# Revit family: Haworth_Encourage_Table
name_source: partatom
category: Furniture
revit_build: Autodesk Revit 2018 (Build: 20170223_1515(x64)
units: mm (PartAtom-declared; Revit-internal decimal feet)

## family parameters
Always vertical = Yes
Cut with Voids When Loaded = No
OmniClass Number = 23.40.70.14.64.21
OmniClass Title = Systems Furniture
Room Calculation Point = No
Shared = No
Work Plane-Based = No

## types (8) — shared parameters
Actual Height = 28 69/256"
Assembly Code = E2020200
Description = Haworth Encourage Table
Leg Finish = Haworth _ Metal _ Stainless Steel
Manufacturer = Haworth
Min/Max Depth = 48 in. / 60 in.
Min/Max Width = 96 in. / 180 in.
Model = TNBO
Power Trough = Yes
Revision Number = 4
Size = Verify Final Dim. w/ Haworth
Top Thickness = 1 27/256"
URL = http://www.haworth.com
URL - Product = https://www.haworth.com
Warranty = http://www.haworth.com

## per-type parameters (varying)
| type | 48d 108w | 48d 96w | 51d 120w | 54d 132w | 54d 144w | 57d 156w | 60d 168w | 60d 180w | Actual Depth | Actual Width | Center Legs | Double Trough Spacing | Modesty Indent | Power Trough Double | Power Trough Single | Support Spacing From Edge | Trough Width |
| TNBO - 48d 96w - With Power | No | Yes | No | No | No | No | No | No | 48" | 96" | No | 17" | 29 3/4" | No | Yes | 26 1/2" | 18" |
| TNBO - 48d 108w - With Power | Yes | No | No | No | No | No | No | No | 48" | 108" | No | 17" | 29 217/256" | No | Yes | 26 153/256" | 24" |
| TNBO - 51d 120w - With Power | No | No | Yes | No | No | No | No | No | 51" | 120" | No | 17" | 36 1/4" | No | Yes | 33" | 30" |
| TNBO - 54d 132w - With Power | No | No | No | Yes | No | No | No | No | 54" | 132" | No | 17" | 37 1/4" | No | Yes | 34" | 36" |
| TNBO - 54d 144w - With Power | No | No | No | No | Yes | No | No | No | 54" | 144" | No | 17" | 37 3/4" | No | Yes | 34 1/2" | 42" |
| TNBO - 57d 156w - With Power | No | No | No | No | No | Yes | No | No | 57" | 156" | Yes | 17" | 39 1/4" | Yes | No | 36" | 24" |
| TNBO - 60d 168w - With Power | No | No | No | No | No | No | Yes | No | 60" | 168" | Yes | 20" | 39 1/4" | Yes | No | 36" | 30" |
| TNBO - 60d 180w - With Power | No | No | No | No | No | No | No | Yes | 60" | 180" | Yes | 23" | 39 1/4" | Yes | No | 36" | 36" |

## geometry (parser evidence)
native form markers: Sweep x12
no freeform markers — native parametric forms only
